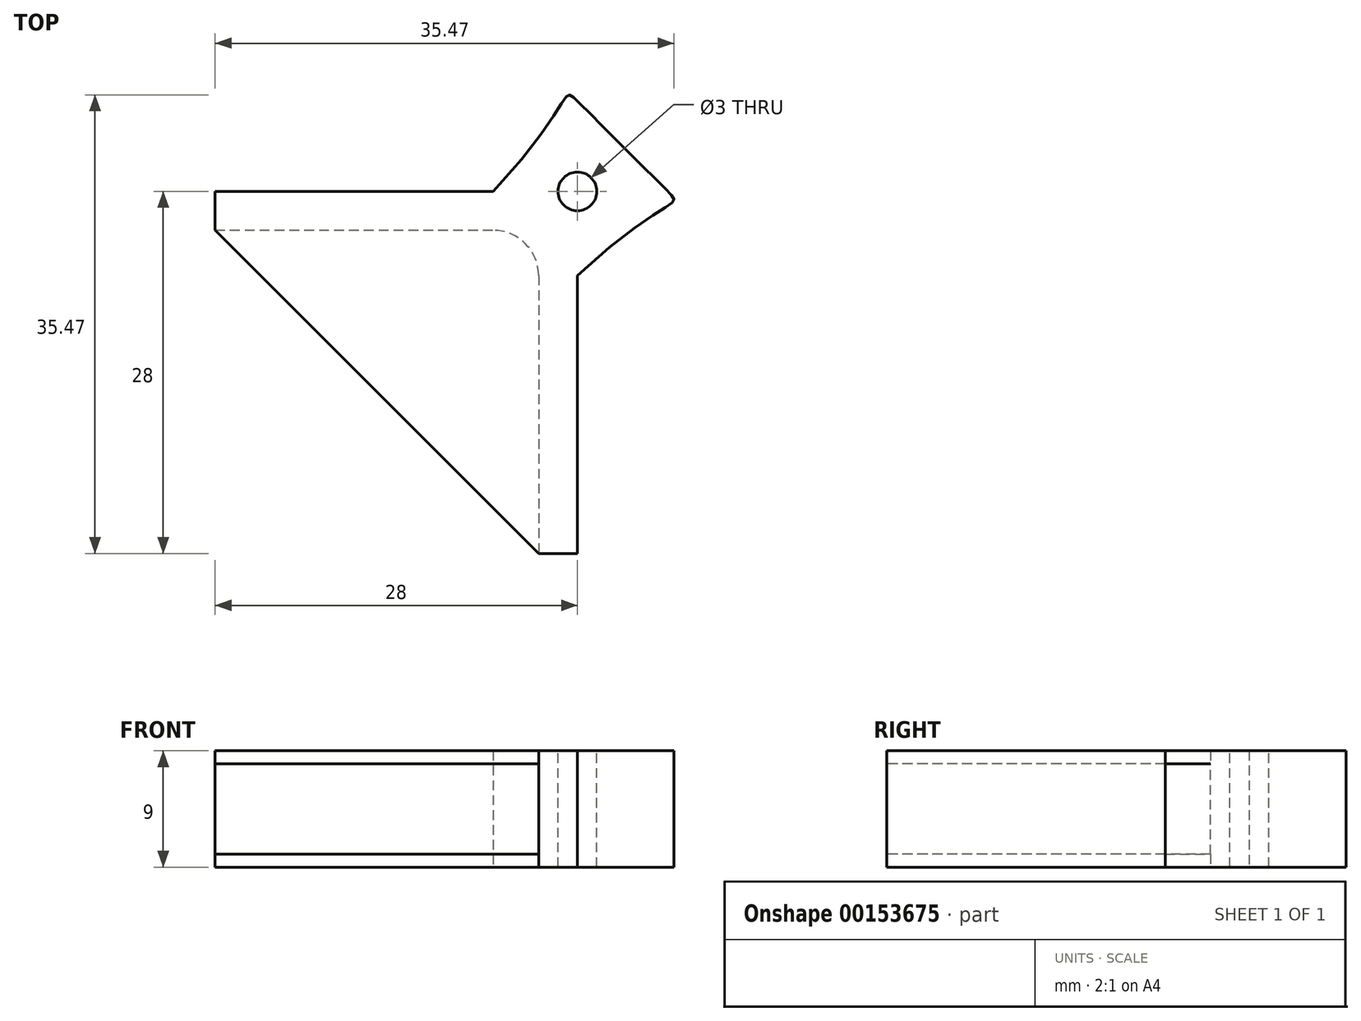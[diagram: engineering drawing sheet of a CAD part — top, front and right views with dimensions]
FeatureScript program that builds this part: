
annotation { "Feature Type Name" : "Feature", "Feature Type Description" : "" }
export const myFeature = defineFeature(function(context is Context, id is Id, definition is map)
    precondition{}
    {
        {
            var Q0;
            Q0=qCreatedBy(makeId("Top.planeOp"),FACE);
            var sketch = newSketch(context, id + "F0", { "sketchPlane" : qUnion([Q0])});
            skLineSegment(sketch, "E0", {"start": v(0, 0) * mm, "end": v(21.5, 0) * mm});
            skLineSegment(sketch, "E1", {"start": v(25, -3.5) * mm, "end": v(25, -25) * mm});
            skLineSegment(sketch, "E2", {"start": v(0, 0) * mm, "end": v(25, -25) * mm});
            skArc(sketch, "E3", {"start": v(25, -3.5) * mm, "mid": v(23.97, -1.03) * mm, "end": v(21.5, 0) * mm});
            skSolve(sketch);
        }
        {
            var Q0;
            Q0=makeQuery(id+"F0.imprint","IMPRINT",FACE,{"disambiguationData":[TD([[makeQuery(id+"F0.imprint","IMPRINT",EDGE,{"derivedFrom":sQuery(id+"F0.wireOp",EDGE,"E0")}),-1.0]])]});
            var sketch = newSketch(context, id + "F1", { "sketchPlane" : qUnion([Q0])});
            skLineSegment(sketch, "E4.0", {"start": v(28, -3.5) * mm, "end": v(28, -25) * mm});
            skArc(sketch, "E4.1", {"start": v(28, -3.5) * mm, "mid": v(26.1, 1.1) * mm, "end": v(21.5, 3) * mm});
            skLineSegment(sketch, "E4.2", {"start": v(0, 3) * mm, "end": v(21.5, 3) * mm});
            skLineSegment(sketch, "E5", {"start": v(0, 3) * mm, "end": v(0, 0) * mm});
            skLineSegment(sketch, "E6", {"start": v(0, 0) * mm, "end": v(25, -25) * mm});
            skLineSegment(sketch, "E7", {"start": v(25, -25) * mm, "end": v(28, -25) * mm});
            skSolve(sketch);
        }
        {
            var Q0;
            Q0=qSketchRegion(id+"F1",true);
            extrude(context, id + "F2", {"entities" : qUnion([Q0]), "depth" : 4.5 * mm, "hasSecondDirection" : true, "secondDirectionOppositeDirection" : true, "secondDirectionDepth" : 4.5 * mm});
        }
        {
            var Q0;
            Q0=qSketchRegion(id+"F0",true);
            extrude(context, id + "F3", {"entities" : qUnion([Q0]), "operationType" : NewBodyOperationType.REMOVE, "oppositeDirection" : true, "depth" : 3.5 * mm, "hasSecondDirection" : true, "secondDirectionOppositeDirection" : false, "secondDirectionDepth" : 3.5 * mm});
        }
        {
            var Q0;
            Q0=makeQuery(id+"F2.opExtrude","CAP_FACE",FACE,{"disambiguationData":[OSD([sQuery(id+"F1.wireOp",EDGE,"E4.0"),sQuery(id+"F1.wireOp",EDGE,"E4.1"),sQuery(id+"F1.wireOp",EDGE,"E4.2"),sQuery(id+"F1.wireOp",EDGE,"E5"),sQuery(id+"F1.wireOp",EDGE,"E6"),sQuery(id+"F1.wireOp",EDGE,"E7")])],"isStart":false});
            var sketch = newSketch(context, id + "F4", { "sketchPlane" : qUnion([Q0])});
            skLineSegment(sketch, "E8", {"start": v(28, -25) * mm, "end": v(28, 10) * mm, "construction": true});
            skLineSegment(sketch, "E9", {"start": v(0, 3) * mm, "end": v(35, 3) * mm, "construction": true});
            skFitSpline(sketch, "E10", {"points": [v(21.5, 3) * mm, v(28, 10) * mm, v(35, 3) * mm, v(28, -3.5) * mm], "startDerivative": vector(58.85, 63.38) * mm, "endDerivative": vector(-63.38, -58.85) * mm});
            skArc(sketch, "E11.0", {"start": v(28, -3.5) * mm, "mid": v(26.1, 1.1) * mm, "end": v(21.5, 3) * mm});
            skCircle(sketch, "E12", {"center": v(28, 3) * mm, "radius": 1.5 * mm});
            skSolve(sketch);
        }
        {
            var Q0;
            Q0=makeQuery(id+"F4.imprint","IMPRINT",FACE,{"disambiguationData":[TD([[makeQuery(id+"F4.imprint","IMPRINT",EDGE,{"derivedFrom":sQuery(id+"F4.wireOp",EDGE,"E10")}),-1.0]])]});
            var Q1;
            Q1=makeQuery(id+"F2.opExtrude","CAP_FACE",FACE,{"disambiguationData":[OSD([sQuery(id+"F1.wireOp",EDGE,"E4.0"),sQuery(id+"F1.wireOp",EDGE,"E4.1"),sQuery(id+"F1.wireOp",EDGE,"E4.2"),sQuery(id+"F1.wireOp",EDGE,"E5"),sQuery(id+"F1.wireOp",EDGE,"E6"),sQuery(id+"F1.wireOp",EDGE,"E7")])],"isStart":true});
            extrude(context, id + "F5", {"entities" : qUnion([Q0]), "operationType" : NewBodyOperationType.ADD, "endBound" : BoundingType.UP_TO_SURFACE, "oppositeDirection" : true, "endBoundEntityFace" : qUnion([Q1]), "depth" : 25 * mm});
        }
    });
